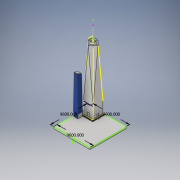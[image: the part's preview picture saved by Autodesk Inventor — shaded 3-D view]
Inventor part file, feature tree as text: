
AUTODESK INVENTOR PART (.ipt)
format: ipt  version: 2018 (Build 220112000, 112)  size: 401,920 bytes
history: native  units: in
note: dims shown in document units (in); Inventor stores cm internally (conversion verified against a paired STEP export)
features: sketch x45, plane x19, extrude x17, other x5, loft x5, fillet x2, projected_geometry x2, delete_face x1
ambient origin geometry x8: Origin, YZ Plane, XZ Plane, XY Plane, X Axis, Y Axis, Z Axis, Center Point
bodies: Solid1 (feature_tree)
feature tree (96):
  other  "Annotations"
  sketch  "Sketch1"  dims[d0=2580.0in d1=2580.0in]
  extrude  "Extrusion1"  Depth=2580.0in
  sketch  "3D Sketch1"
  sketch  "Sketch5"  dims[d31=13416.0in d32=13416.0in]
  sketch  "Sketch6"  dims[d33=90.0deg d34=13416.0in]
  plane  "Work Plane1"
  sketch  "Sketch7"  dims[d35=13416.0in d36=13416.0in]
  plane  "Work Plane2"
  plane  "Work Plane3"
  sketch  "Sketch8"  dims[d37=13416.0in d39=13416.0in]
  sketch  "Sketch9"  dims[d40=0.5805in d41=13416.0in]
  plane  "Work Plane4"
  sketch  "Sketch10"  dims[d42=0.6563in d43=0.0in d44=90.0deg]
  plane  "Work Plane5"
  loft  "Loft1"
  loft  "Loft2"
  extrude  "Extrusion5"  Depth=13416.0in
  sketch  "Sketch13"  dims[d49=0.0in d50=90.0deg d55=1.0in d56=0.0in]
  plane  "Work Plane6"
  extrude  "Extrusion6"  Depth=13416.0in
  plane  "Work Plane7"
  extrude  "Extrusion7"  Depth=13416.0in
  plane  "Work Plane8"
  plane  "Work Plane9"
  sketch  "Sketch16"  dims[d67=1500.0in d68=600.0in d69=0.0in]
  extrude  "Extrusion8"  Depth=13416.0in
  extrude  "Extrusion9"  TaperAngle=0.0deg  [1 undecoded]
  extrude  "Extrusion10"  TaperAngle=0.0deg  [1 undecoded]
  extrude  "Extrusion11"  Depth=1.0in TaperAngle=0.0deg
  delete_face  "Delete Face1"
  extrude  "Extrusion12"  Depth=1.0in TaperAngle=0.0deg
  sketch  "Sketch22"  dims[d88=200.0in d91=200.0in]
  sketch  "Sketch23"  dims[d92=0.0in d93=90.0deg d94=0.0in d95=90.0deg]
  sketch  "Sketch24"  dims[d96=669.0in d97=180.0deg d98=36.0in d99=0.0in]
  sketch  "Sketch25"  dims[d100=36.0in d101=0.0in d102=36.0in d103=0.0in d110=0.0in d111=90.0deg]
  sketch  "Sketch26"  dims[d112=0.0in d113=90.0deg d116=9600.0in]
  fillet  "Fillet1"  Radius=1.0in
  sketch  "Sketch27"  dims[d117=9600.0in d118=9600.0in]
  plane  "Work Plane11"
  loft  "Loft3"
  sketch  "Sketch29"  dims[d124=300.0in]
  extrude  "Extrusion14"  Depth=600.0in TaperAngle=0.0deg
  extrude  "Extrusion15"  Depth=400.0in
  sketch  "Sketch31"  dims[d126=1.0in d127=0.0in]
  extrude  "Extrusion16"  Depth=669.0in
  sketch  "Sketch32"  dims[d128=90.0deg]
  sketch  "Sketch33"  dims[d222=90.0deg]
  plane  "Work Plane12"
  sketch  "Sketch34"  dims[d223=200.0in d224=0.0in]
  loft  "Loft4"
  plane  "Work Plane13"
  sketch  "Sketch35"  dims[d225=200.0in d226=0.0in]
  extrude  "Extrusion19"  Depth=200.0in
  extrude  "Extrusion20"  TaperAngle=0.0deg  [1 undecoded]
  plane  "Work Plane14"
  sketch  "Sketch37"  dims[d228=90.0deg]
  sketch  "Sketch38"  dims[d237=1000.0in d238=0.0in]
  sketch  "Sketch39"  dims[d247=0.0in d248=90.0deg]
  sketch  "Sketch48"  dims[d249=0.0in d250=90.0deg]
  plane  "Work Plane15"
  sketch  "Sketch49"  dims[d114=0.2753in d115=21692.8722in]
  extrude  "Extrusion32"  Depth=36.0in TaperAngle=0.0deg
  extrude  "Extrusion33"  Depth=36.0in TaperAngle=0.0deg
  fillet  "Fillet2"  [1 undecoded]
  plane  "Work Plane16"
  sketch  "Sketch57"
  extrude  "Extrusion37"  Depth=9600.0in
  plane  "Work Plane19"
  sketch  "Sketch59"
  sketch  "Sketch60"
  plane  "Work Plane20"
  sketch  "Sketch61"
  plane  "Work Plane22"
  sketch  "Sketch65"
  plane  "Work Plane23"
  sketch  "Sketch66"
  loft  "Loft7"
  sketch  "Sketch2"  dims[d2=3000.0in d3=0.0in d30=90.0deg]
  sketch  "Sketch12"  dims[d45=0.0in d46=90.0deg d47=0.0in d48=90.0deg]
  sketch  "Sketch14"  dims[d57=1.0in d58=0.0in d59=1.0in d60=0.0in d61=1.0in d62=0.0in]
  sketch  "Sketch15"  dims[d63=1.0in d64=0.0in d65=120.0in d66=0.0in]
  sketch  "Sketch17"  dims[d71=400.0in d72=400.0in]
  sketch  "Sketch18"  dims[d73=1200.0in d74=0.0in d85=669.0in]
  other  "Srf1"
  sketch  "Sketch19"  dims[d86=669.0in d87=180.0deg]
  sketch  "Sketch28"  dims[d119=500.0in d120=0.0in]
  other  "Edges1"
  other  "Edges2"
  sketch  "Sketch36"  dims[d227=111.25in]
  sketch  "Sketch58"
  projected_geometry  "Projected Loop1"
  sketch  "Sketch67"
  sketch  "Sketch30"  dims[d125=300.0in]
  projected_geometry  "Project Cut Edges1"
  other  "Linear Dimension 2"
note: 4 required parameter values undecoded (feature->parameter linkage not recoverable at this tier; creation-order binding heuristic only, values carry confidence <= 0.55)
